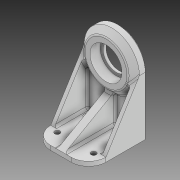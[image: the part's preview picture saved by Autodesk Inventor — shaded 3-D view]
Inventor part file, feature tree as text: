
AUTODESK INVENTOR PART (.ipt)
format: ipt  version: 2020 (Build 240168000, 168)  size: 398,848 bytes
history: native  units: mm
features: extrude x7, sketch x7, fillet x2, chamfer x2, mirror x1, projected_geometry x1
ambient origin geometry x8: Origin, YZ Plane, XZ Plane, XY Plane, X Axis, Y Axis, Z Axis, Center Point
bodies: Solid1 (feature_tree)
feature tree (20):
  extrude  "Extrusion1"  Depth=3.0mm
  extrude  "Extrusion2"  Depth=38.0mm
  fillet  "Fillet1"  Radius=38.0mm
  extrude  "Extrusion6"  Depth=40.0mm
  chamfer  "Chamfer1"  [1 undecoded]
  extrude  "Extrusion3"  Depth=12.0mm
  extrude  "Extrusion4"  Depth=25.0mm
  extrude  "Extrusion5"  TaperAngle=0.0deg  [1 undecoded]
  mirror  "Mirror1"
  fillet  "Fillet2"  Radius=2.5mm
  extrude  "Extrusion7"  Depth=2.0mm TaperAngle=0.0deg
  chamfer  "Chamfer2"  Distance=1.5mm
  sketch  "Sketch1"  dims[d0=5.0mm d1=3.0mm]
  sketch  "Sketch2"  dims[d2=40.0mm d3=80.0mm d4=38.0mm d5=0.0mm]
  projected_geometry  "Projected Loop1"
  sketch  "Sketch3"  dims[d6=22.0mm d7=40.0mm d8=0.0mm d9=0.0mm]
  sketch  "Sketch4"  dims[d10=12.0mm d11=20.0mm]
  sketch  "Sketch5"  dims[d12=20.0mm d13=25.0mm]
  sketch  "Sketch6"  dims[d14=3.5mm d15=0.0mm d16=0.0mm d17=2.5mm d18=0.0mm]
  sketch  "Sketch7"  dims[d19=6.0mm d20=5.0mm d21=0.0mm d22=1.5mm d23=4.0mm d24=0.0mm d25=30.0mm d26=4.0mm d27=2.0mm d28=45.0deg d29=2.0mm d30=2.0mm d31=0.0mm d32=1.0mm d33=2.0mm d34=45.0deg]
note: 2 required parameter values undecoded (feature->parameter linkage not recoverable at this tier; creation-order binding heuristic only, values carry confidence <= 0.55)
